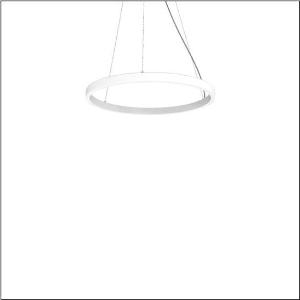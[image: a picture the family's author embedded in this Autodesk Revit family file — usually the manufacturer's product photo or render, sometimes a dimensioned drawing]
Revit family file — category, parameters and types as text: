
# Revit family: silica_21_ring-o_5pjbo2d1004a
name_source: partatom
category: Lighting Fixtures
units: mm (PartAtom-declared; Revit-internal decimal feet)

## family parameters
Cut with Voids When Loaded = No
Host = Face
Light Source = No
Part Type = Normal
Room Calculation Point = No
Round Connector Dimension = Use Diameter
Shared = No

## types (1)
- Silica 21 Ring-O (1 x LED, 4700 lm, 80 W, 3000K)
    Apparent Load = 80 VA
    CIE Flux Codes = 2 16 49 50 100
    Color Rendering = 80
    Color Temperature = 3000K
    Default Elevation = 1800 mm
    Description = Silica 21 Ring-O, suspended luminaire, of PMMA, frosted, light emission: outer ring side luminous distribution, primary light characteristic: symmetric, installation type: suspended mounting, LED, rated luminous flux: 4.700lm, luminous efficacy: 59lm/W, light colour: 830, colour temperature: 3000K, control gear: DALI 2, with terminal, 5-pole, mains connection: 230V, AC/DC, 0/50..60Hz, rated input power: 80W, housing, of extruded aluminium section, traffic white (RAL 9016), diameter: 810mm, ceiling canopy, traffic white (RAL 9016), protection rating (lamp compartment): IP40, insulation class (complete): insulation class I (protective earthing), certification: CE, impact resistance: IK02, permissible operating ambient temperature: 0..+35°C, packaging unit: 1 piece
    Height = 48 mm  [stored 0.15748 ft]
    Lamp = 1 x LED
    Lamp Light Flux = 4700 lm
    Lamp Power = 80 W
    Lamp count = 1
    Length = 810 mm
    Luminous efficacy = 59 lm/W
    Manufacturer = Siteco
    ModVariant = No
    Model = 5PJBO2D1004A
    Mounting Place = Ceiling
    Mounting Type = Pendant
    Number of Poles = 1
    OnlyDefault = Yes
    Power Factor = 1
    Product Name = Silica 21 Ring-O
    Product group = suspended luminaire
    ProductGroupID = 904
    Protection Class = Protection class I
    Protection Degree = IP 40
    RLX_Detail_Level = 1
    RLX_Emergency_Light_Flux = 0 lm
    RLX_Emergency_Type = 0
    RLX_Emergency_Type_DB = No
    RlxData = <blob elided: 11993 chars, md5=659b4749>
    Socket = socket
    Standby Power = 0 W
    System Light Flux = 4700 lm
    System Power = 80 W
    Type Comments = Product without accessories
    Type Image = l_1258383.jpg
    URL = http://relux.com
    VarID = ---
    Voltage = 0 V
    Weight = 0.00 kg
    Width = 0 mm  [stored 0 ft]

note: [stored X ft] marks values corroborated as IEEE doubles in the binary element streams (Revit-internal decimal feet)

## geometry (parser evidence)
native form markers: Sweep x12
no freeform markers — native parametric forms only
